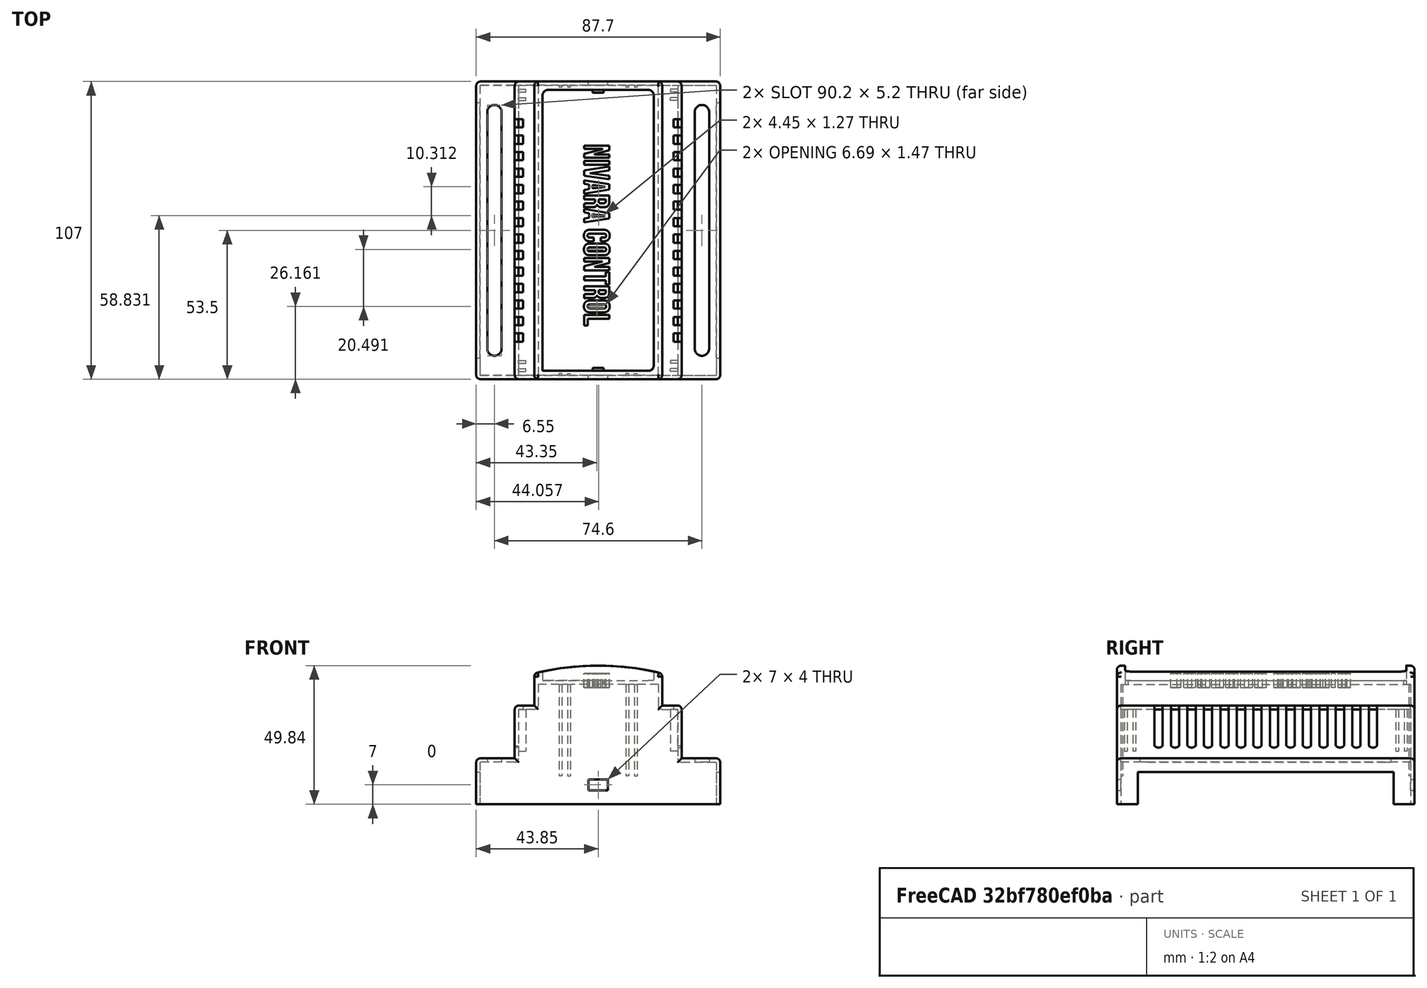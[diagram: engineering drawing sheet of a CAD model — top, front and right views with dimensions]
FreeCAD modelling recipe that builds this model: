
FCSTD DOCUMENT  (FreeCAD 1.0R39285 (Git))
Label: Diseño de la Pieza con su Etiqueta (2023-1283)
License: All rights reserved
LicenseURL: https://en.wikipedia.org/wiki/All_rights_reserved
objects: Sketcher::SketchObject×15, PartDesign::Pad×9, PartDesign::Mirrored×7, PartDesign::Pocket×6, PartDesign::Fillet×4, PartDesign::Thickness×2, PartDesign::Plane×1, PartDesign::Body×1, Part::Box×1, Part::Part2DObjectPython×1, Part::Extrusion×1, Part::Cut×1
note: 113 computed .brp shape members not serialized (recipe doc carries the construction recipe); baked Part::Feature solids carry a one-line shape summary decoded from their .brp

FEATURE [Sketcher::SketchObject] Sketch
  ArcFitTolerance = 1e-06
  AttachmentSupport = -> [XZ_Plane001]
  FullyConstrained = true
  MakeInternals = false
  MapMode = 5
  Placement = pos=(0,0,0) rot=(1,0,0;1.5708rad)
  sketch-geometry (12):
    g0: LineSegment StartX=-43.85 StartY=0 StartZ=0 EndX=43.85 EndY=0 EndZ=0
    g1: LineSegment StartX=-43.85 StartY=0 StartZ=0 EndX=-43.85 EndY=16.54 EndZ=0
    g2: LineSegment StartX=43.85 StartY=0 StartZ=0 EndX=43.85 EndY=16.54 EndZ=0
    g3: LineSegment StartX=-43.85 StartY=16.54 StartZ=0 EndX=-30 EndY=16.54 EndZ=0
    g4: LineSegment StartX=43.85 StartY=16.54 StartZ=0 EndX=30 EndY=16.54 EndZ=0
    g5: LineSegment StartX=-30 StartY=16.54 StartZ=0 EndX=-30 EndY=35.54 EndZ=0
    g6: LineSegment StartX=30 StartY=16.54 StartZ=0 EndX=30 EndY=35.54 EndZ=0
    g7: LineSegment StartX=-30 StartY=35.54 StartZ=0 EndX=-23 EndY=35.54 EndZ=0
    g8: LineSegment StartX=30 StartY=35.54 StartZ=0 EndX=23 EndY=35.54 EndZ=0
    g9: LineSegment StartX=23 StartY=35.54 StartZ=0 EndX=23 EndY=44.54 EndZ=0
    g10: LineSegment StartX=-23 StartY=35.54 StartZ=0 EndX=-23 EndY=44.54 EndZ=0
    g11: LineSegment StartX=-23 StartY=44.54 StartZ=0 EndX=23 EndY=44.54 EndZ=0
  constraints (36):
    c: Distance(g0) = 87.7
    c: PointOnObject(g0,g-1)
    c: PointOnObject(g0,g-1)
    c: Vertical(g1)
    c: Coincident(g1,g0)
    c: Vertical(g2)
    c: Coincident(g2,g0)
    c: Distance(g3) = 13.85
    c: Horizontal(g3)
    c: Coincident(g3,g1)
    c: Distance(g4) = 13.85
    c: Horizontal(g4)
    c: Coincident(g4,g2)
    c: Vertical(g5)
    c: Coincident(g5,g3)
    c: Vertical(g6)
    c: Coincident(g6,g4)
    c: Distance(g7) = 7
    c: Horizontal(g7)
    c: Coincident(g7,g5)
    c: Distance(g8) = 7
    c: Horizontal(g8)
    c: Coincident(g8,g6)
    c: Vertical(g9)
    c: Coincident(g9,g8)
    c: Vertical(g10)
    c: Coincident(g10,g7)
    c: Coincident(g11,g10)
    c: Coincident(g11,g9)
    c: Equal(g1,g2)
    c: Equal(g5,g6)
    c: Equal(g10,g9)
    c: Distance(g0,g11) = 44.54
    c: DistanceY(g1,g1) = 16.54
    c: Distance(g5,g0) = 35.54
    c: Distance(g10,g-2) = 23
FEATURE [PartDesign::Pad] Pad
  Direction = (0,-1,2e-16)
  Length = 107
  Length2 = 10
  Placement = pos=(0,0,0) rot=(1,0,0;1.5708rad)
  Profile = -> Sketch
  ReferenceAxis = -> Sketch [N_Axis]
  Refine = true
  Suppressed = false
  Type = 0
FEATURE [PartDesign::Thickness] Thickness
  Base = -> Pad
  BaseFeature = -> Pad
  Intersection = false
  Join = 0
  Mode = 0
  Placement = pos=(0,0,0) rot=(1,0,0;1.5708rad)
  Refine = true
  Reversed = true
  SupportTransform = false
  Suppressed = false
  Value = 1.4
FEATURE [PartDesign::Thickness] Thickness001
  Base = -> Thickness [Face1]
  BaseFeature = -> Thickness
  Intersection = false
  Join = 0
  Mode = 0
  Refine = true
  Reversed = true
  SupportTransform = false
  Suppressed = false
  Value = 1.4
FEATURE [Sketcher::SketchObject] Sketch001
  ArcFitTolerance = 1e-06
  AttachmentSupport = -> [Thickness001]
  FullyConstrained = true
  MakeInternals = false
  MapMode = 5
  Placement = pos=(-43.85,0,0) rot=(0.57735,-0.57735,-0.57735;2.0944rad)
  sketch-geometry (4):
    g0: LineSegment StartX=7.575 StartY=0 StartZ=0 EndX=99.425 EndY=0 EndZ=0
    g1: LineSegment StartX=99.425 StartY=0 StartZ=0 EndX=99.425 EndY=11.6 EndZ=0
    g2: LineSegment StartX=99.425 StartY=11.6 StartZ=0 EndX=7.575 EndY=11.6 EndZ=0
    g3: LineSegment StartX=7.575 StartY=11.6 StartZ=0 EndX=7.575 EndY=0 EndZ=0
  constraints (12):
    c: Coincident(g0,g1)
    c: Coincident(g1,g2)
    c: Coincident(g2,g3)
    c: Coincident(g3,g0)
    c: Horizontal(g0)
    c: Horizontal(g2)
    c: Vertical(g1)
    c: Vertical(g3)
    c: PointOnObject(g0,g-1)
    c: DistanceX(g2,g2) = 91.85
    c: DistanceY(g1,g1) = 11.6
    c: DistanceX(g-1,g0) = 7.575
FEATURE [PartDesign::Pocket] Pocket
  BaseFeature = -> Thickness001
  Direction = (1,0,0)
  Length = 5
  Length2 = 5
  Profile = -> Sketch001
  ReferenceAxis = -> Sketch001 [N_Axis]
  Refine = true
  Suppressed = false
  Type = 1
FEATURE [Sketcher::SketchObject] Sketch002
  ArcFitTolerance = 1e-06
  AttachmentSupport = -> [Pocket]
  FullyConstrained = true
  MakeInternals = false
  MapMode = 5
  Placement = pos=(0,4.2e-15,0) rot=(0,0.707107,0.707107;3.14159rad)
  sketch-geometry (4):
    g0: LineSegment StartX=-23 StartY=44.54 StartZ=0 EndX=23 EndY=44.54 EndZ=0
    g1: LineSegment StartX=-23 StartY=44.54 StartZ=0 EndX=-23 EndY=47.04 EndZ=0
    g2: LineSegment StartX=23 StartY=44.54 StartZ=0 EndX=23 EndY=47.04 EndZ=0
    g3: ArcOfCircle CenterX=1.7e-15 CenterY=-46.0243 CenterZ=0 NormalX=0 NormalY=0 NormalZ=1 AngleXU=0 Radius=95.8643 StartAngle=1.32851 EndAngle=1.81308
  constraints (13):
    c: Distance(g0) = 46
    c: Horizontal(g0)
    c: Distance(g-1,g0) = 44.54
    c: Distance(g0,g-2) = 23
    c: Distance(g1) = 2.5
    c: Coincident(g1,g0)
    c: Vertical(g1)
    c: Distance(g2) = 2.5
    c: Coincident(g2,g0)
    c: Vertical(g2)
    c: Coincident(g3,g1)
    c: Coincident(g3,g2)
    c: Distance(g3,g0) = -5.3
FEATURE [PartDesign::Pad] Pad001
  BaseFeature = -> Pocket
  Direction = (0,1,-2e-16)
  Length = 107
  Length2 = 10
  Profile = -> Sketch002
  ReferenceAxis = -> Sketch002 [N_Axis]
  Refine = true
  Suppressed = false
  Type = 0
FEATURE [Sketcher::SketchObject] Sketch003
  ArcFitTolerance = 1e-06
  AttachmentSupport = -> [Pad001]
  ExternalGeometry = -> [Pad001]
  FullyConstrained = true
  MakeInternals = false
  MapMode = 5
  Placement = pos=(0,4.2e-15,0) rot=(0,0.707107,0.707107;3.14159rad)
  sketch-geometry (4):
    g0: LineSegment StartX=-23 StartY=44.54 StartZ=0 EndX=-23 EndY=47.04 EndZ=0
    g1: LineSegment StartX=23 StartY=44.54 StartZ=0 EndX=23 EndY=47.04 EndZ=0
    g2: ArcOfCircle CenterX=4.82e-14 CenterY=-46.0243 CenterZ=0 NormalX=0 NormalY=0 NormalZ=1 AngleXU=0 Radius=95.8643 StartAngle=1.32851 EndAngle=1.81308
    g3: LineSegment StartX=-23 StartY=44.54 StartZ=0 EndX=23 EndY=44.54 EndZ=0
  constraints (9):
    c: Distance(g0) = 2.5
    c: Coincident(g2,g0)
    c: Coincident(g2,g1)
    c: Coincident(g3,g-3)
    c: Coincident(g3,g-3)
    c: Perpendicular(g0,g3) = 4.71239
    c: Distance(g2,g3) = -5.3
    c: Perpendicular(g1,g3) = 4.71239
    c: DistanceY(g1,g1) = 2.5
FEATURE [PartDesign::Pad] Pad002
  BaseFeature = -> Pad001
  Direction = (0,1,-2e-16)
  Length = 3
  Length2 = 10
  Profile = -> Sketch003
  ReferenceAxis = -> Sketch003 [N_Axis]
  Refine = true
  Reversed = true
  Suppressed = false
  Type = 0
FEATURE [Sketcher::SketchObject] Sketch004
  ArcFitTolerance = 1e-06
  AttachmentSupport = -> [Pad002]
  ExternalGeometry = -> [Pad002]
  FullyConstrained = true
  MakeInternals = false
  MapMode = 5
  Placement = pos=(0,-107,0) rot=(1,0,0;1.5708rad)
  sketch-geometry (4):
    g0: LineSegment StartX=-23 StartY=44.54 StartZ=0 EndX=23 EndY=44.54 EndZ=0
    g1: LineSegment StartX=23 StartY=44.54 StartZ=0 EndX=23 EndY=47.04 EndZ=0
    g2: LineSegment StartX=-23 StartY=44.54 StartZ=0 EndX=-23 EndY=47.04 EndZ=0
    g3: ArcOfCircle CenterX=3.7756e-12 CenterY=-46.0243 CenterZ=0 NormalX=0 NormalY=0 NormalZ=1 AngleXU=0 Radius=95.8643 StartAngle=1.32851 EndAngle=1.81308
  constraints (9):
    c: Coincident(g0,g-5)
    c: Coincident(g0,g-6)
    c: Coincident(g1,g0)
    c: Coincident(g1,g-6)
    c: Coincident(g2,g0)
    c: Coincident(g2,g-5)
    c: Coincident(g3,g2)
    c: Coincident(g3,g1)
    c: Tangent(g3,g-4)
FEATURE [PartDesign::Pad] Pad003
  BaseFeature = -> Pad002
  Direction = (0,-1,2e-16)
  Length = 3
  Length2 = 10
  Profile = -> Sketch004
  ReferenceAxis = -> Sketch004 [N_Axis]
  Refine = true
  Reversed = true
  Suppressed = false
  Type = 0
FEATURE [Sketcher::SketchObject] Sketch005
  ArcFitTolerance = 1e-06
  AttachmentSupport = -> [Pad003]
  ExternalGeometry = -> [Pad003]
  FullyConstrained = true
  MakeInternals = false
  MapMode = 5
  Placement = pos=(23,-8.5e-15,1.304e-13) rot=(0.57735,0.57735,0.57735;2.0944rad)
  sketch-geometry (4):
    g0: LineSegment StartX=-104 StartY=49.84 StartZ=0 EndX=-104 EndY=44.54 EndZ=0
    g1: LineSegment StartX=-104 StartY=44.54 StartZ=0 EndX=-3 EndY=44.54 EndZ=0
    g2: LineSegment StartX=-3 StartY=49.84 StartZ=0 EndX=-3 EndY=44.54 EndZ=0
    g3: LineSegment StartX=-104 StartY=49.84 StartZ=0 EndX=-3 EndY=49.84 EndZ=0
  constraints (8):
    c: Coincident(g0,g-5)
    c: Coincident(g0,g-3)
    c: Coincident(g1,g0)
    c: Coincident(g1,g-3)
    c: Coincident(g2,g-4)
    c: Coincident(g2,g1)
    c: Coincident(g3,g0)
    c: Coincident(g3,g2)
FEATURE [PartDesign::Pad] Pad004
  BaseFeature = -> Pad003
  Direction = (1,0,5.8e-15)
  Length = 3
  Length2 = 10
  Profile = -> Sketch005
  ReferenceAxis = -> Sketch005 [N_Axis]
  Refine = true
  Reversed = true
  Suppressed = false
  Type = 0
FEATURE [PartDesign::Mirrored] Mirrored
  BaseFeature = -> Pad004
  MirrorPlane = -> YZ_Plane001
  Originals = -> [Pad004]
  Refine = true
  Suppressed = false
  TransformMode = 0
FEATURE [Sketcher::SketchObject] Sketch006
  ArcFitTolerance = 1e-06
  AttachmentSupport = -> [Mirrored]
  FullyConstrained = true
  MakeInternals = false
  MapMode = 5
  Placement = pos=(0,7.3e-15,16.54) rot=(0,0,1;0rad)
  sketch-geometry (4):
    g0: ArcOfCircle CenterX=37.3 CenterY=-11 CenterZ=0 NormalX=0 NormalY=0 NormalZ=1 AngleXU=0 Radius=2.6 StartAngle=2.2037e-12 EndAngle=3.14159
    g1: ArcOfCircle CenterX=37.3 CenterY=-96 CenterZ=0 NormalX=0 NormalY=0 NormalZ=1 AngleXU=0 Radius=2.6 StartAngle=3.14159 EndAngle=6.28319
    g2: LineSegment StartX=39.9 StartY=-11 StartZ=0 EndX=39.9 EndY=-96 EndZ=0
    g3: LineSegment StartX=34.7 StartY=-11 StartZ=0 EndX=34.7 EndY=-96 EndZ=0
  constraints (10):
    c: Tangent(g0,g2) = 1.5708
    c: Tangent(g0,g3) = -1.5708
    c: Tangent(g1,g2) = 1.5708
    c: Tangent(g1,g3) = -1.5708
    c: Equal(g0,g1)
    c: Vertical(g2)
    c: Distance(g2,g3) = 5.2
    c: DistanceY(g2,g2) = 85
    c: Distance(g0,g-2) = 37.3
    c: Distance(g0,g-1) = 11
FEATURE [PartDesign::Pocket] Pocket001
  BaseFeature = -> Mirrored
  Direction = (0,0,-1)
  Length = 5
  Length2 = 5
  Profile = -> Sketch006
  ReferenceAxis = -> Sketch006 [N_Axis]
  Refine = true
  Suppressed = false
  Type = 0
FEATURE [PartDesign::Mirrored] Mirrored001
  BaseFeature = -> Pocket001
  MirrorPlane = -> YZ_Plane001
  Originals = -> [Pocket001]
  Refine = true
  Suppressed = false
  TransformMode = 0
FEATURE [Sketcher::SketchObject] Sketch007
  ArcFitTolerance = 1e-06
  AttachmentSupport = -> [Mirrored001]
  ExternalGeometry = -> [Mirrored001]
  FullyConstrained = true
  MakeInternals = false
  MapMode = 5
  Placement = pos=(30,0,0) rot=(0.57735,0.57735,0.57735;2.0944rad)
  sketch-geometry (57):
    g0: LineSegment [constr] StartX=-53.5 StartY=35.54 StartZ=0 EndX=-53.5 EndY=16.54 EndZ=0
    g1: LineSegment StartX=-16.4625 StartY=35.54 StartZ=0 EndX=-13.4995 EndY=35.54 EndZ=0
    g2: LineSegment StartX=-13.4995 StartY=35.54 StartZ=0 EndX=-13.4995 EndY=21.04 EndZ=0
    g3: LineSegment StartX=-16.4625 StartY=35.54 StartZ=0 EndX=-16.4625 EndY=21.04 EndZ=0
    g4: ArcOfCircle CenterX=-14.981 CenterY=22.3836 CenterZ=0 NormalX=0 NormalY=0 NormalZ=1 AngleXU=0 Radius=2 StartAngle=3.8782 EndAngle=5.54658
    g5: LineSegment StartX=-22.3885 StartY=35.54 StartZ=0 EndX=-19.4255 EndY=35.54 EndZ=0
    g6: LineSegment StartX=-19.4255 StartY=35.54 StartZ=0 EndX=-19.4255 EndY=21.04 EndZ=0
    g7: LineSegment StartX=-22.3885 StartY=35.54 StartZ=0 EndX=-22.3885 EndY=21.04 EndZ=0
    g8: ArcOfCircle CenterX=-20.907 CenterY=22.3836 CenterZ=0 NormalX=0 NormalY=0 NormalZ=1 AngleXU=0 Radius=2 StartAngle=3.8782 EndAngle=5.54658
    g9: LineSegment StartX=-28.3145 StartY=35.54 StartZ=0 EndX=-25.3515 EndY=35.54 EndZ=0
    g10: LineSegment StartX=-25.3515 StartY=35.54 StartZ=0 EndX=-25.3515 EndY=21.04 EndZ=0
    g11: LineSegment StartX=-28.3145 StartY=35.54 StartZ=0 EndX=-28.3145 EndY=21.04 EndZ=0
    g12: ArcOfCircle CenterX=-26.833 CenterY=22.3836 CenterZ=0 NormalX=0 NormalY=0 NormalZ=1 AngleXU=0 Radius=2 StartAngle=3.8782 EndAngle=5.54658
    g13: LineSegment StartX=-34.2405 StartY=35.54 StartZ=0 EndX=-31.2775 EndY=35.54 EndZ=0
    g14: LineSegment StartX=-34.2405 StartY=35.54 StartZ=0 EndX=-34.2405 EndY=21.04 EndZ=0
    g15: LineSegment StartX=-31.2775 StartY=35.54 StartZ=0 EndX=-31.2775 EndY=21.04 EndZ=0
    g16: ArcOfCircle CenterX=-32.759 CenterY=22.3836 CenterZ=0 NormalX=0 NormalY=0 NormalZ=1 AngleXU=0 Radius=2 StartAngle=3.8782 EndAngle=5.54658
    g17: LineSegment StartX=-40.1665 StartY=35.54 StartZ=0 EndX=-37.2035 EndY=35.54 EndZ=0
    g18: LineSegment StartX=-37.2035 StartY=35.54 StartZ=0 EndX=-37.2035 EndY=21.04 EndZ=0
    g19: LineSegment StartX=-40.1665 StartY=35.54 StartZ=0 EndX=-40.1665 EndY=21.04 EndZ=0
    g20: ArcOfCircle CenterX=-38.685 CenterY=22.3836 CenterZ=0 NormalX=0 NormalY=0 NormalZ=1 AngleXU=0 Radius=2 StartAngle=3.8782 EndAngle=5.54658
    g21: LineSegment StartX=-46.0925 StartY=35.54 StartZ=0 EndX=-43.1295 EndY=35.54 EndZ=0
    g22: LineSegment StartX=-43.1295 StartY=35.54 StartZ=0 EndX=-43.1295 EndY=21.04 EndZ=0
    g23: LineSegment StartX=-46.0925 StartY=35.54 StartZ=0 EndX=-46.0925 EndY=21.04 EndZ=0
    g24: ArcOfCircle CenterX=-44.611 CenterY=22.3836 CenterZ=0 NormalX=0 NormalY=0 NormalZ=1 AngleXU=0 Radius=2 StartAngle=3.8782 EndAngle=5.54658
    g25: LineSegment StartX=-52.0185 StartY=35.54 StartZ=0 EndX=-49.0555 EndY=35.54 EndZ=0
    g26: LineSegment StartX=-49.0555 StartY=35.54 StartZ=0 EndX=-49.0555 EndY=21.04 EndZ=0
    g27: LineSegment StartX=-52.0185 StartY=35.54 StartZ=0 EndX=-52.0185 EndY=21.04 EndZ=0
    g28: ArcOfCircle CenterX=-50.537 CenterY=22.3836 CenterZ=0 NormalX=0 NormalY=0 NormalZ=1 AngleXU=0 Radius=2 StartAngle=3.8782 EndAngle=5.54658
    g29: LineSegment StartX=-57.9445 StartY=35.54 StartZ=0 EndX=-54.9815 EndY=35.54 EndZ=0
    g30: LineSegment StartX=-54.9815 StartY=35.54 StartZ=0 EndX=-54.9815 EndY=21.04 EndZ=0
    g31: LineSegment StartX=-57.9445 StartY=35.54 StartZ=0 EndX=-57.9445 EndY=21.04 EndZ=0
    g32: ArcOfCircle CenterX=-56.463 CenterY=22.3836 CenterZ=0 NormalX=0 NormalY=0 NormalZ=1 AngleXU=0 Radius=2 StartAngle=3.8782 EndAngle=5.54658
    g33: LineSegment StartX=-63.8705 StartY=35.54 StartZ=0 EndX=-60.9075 EndY=35.54 EndZ=0
    g34: LineSegment StartX=-60.9075 StartY=35.54 StartZ=0 EndX=-60.9075 EndY=21.04 EndZ=0
    g35: LineSegment StartX=-63.8705 StartY=35.54 StartZ=0 EndX=-63.8705 EndY=21.04 EndZ=0
    g36: ArcOfCircle CenterX=-62.389 CenterY=22.3836 CenterZ=0 NormalX=0 NormalY=0 NormalZ=1 AngleXU=0 Radius=2 StartAngle=3.8782 EndAngle=5.54658
    g37: LineSegment StartX=-69.7965 StartY=35.54 StartZ=0 EndX=-66.8335 EndY=35.54 EndZ=0
    g38: LineSegment StartX=-66.8335 StartY=35.54 StartZ=0 EndX=-66.8335 EndY=21.04 EndZ=0
    g39: LineSegment StartX=-69.7965 StartY=35.54 StartZ=0 EndX=-69.7965 EndY=21.04 EndZ=0
    g40: ArcOfCircle CenterX=-68.315 CenterY=22.3836 CenterZ=0 NormalX=0 NormalY=0 NormalZ=1 AngleXU=0 Radius=2 StartAngle=3.8782 EndAngle=5.54658
    g41: LineSegment StartX=-75.7225 StartY=35.54 StartZ=0 EndX=-72.7595 EndY=35.54 EndZ=0
    g42: LineSegment StartX=-72.7595 StartY=35.54 StartZ=0 EndX=-72.7595 EndY=21.04 EndZ=0
    g43: LineSegment StartX=-75.7225 StartY=35.54 StartZ=0 EndX=-75.7225 EndY=21.04 EndZ=0
    g44: ArcOfCircle CenterX=-74.241 CenterY=22.3836 CenterZ=0 NormalX=0 NormalY=0 NormalZ=1 AngleXU=0 Radius=2 StartAngle=3.8782 EndAngle=5.54658
    g45: LineSegment StartX=-81.6485 StartY=35.54 StartZ=0 EndX=-78.6855 EndY=35.54 EndZ=0
    g46: LineSegment StartX=-78.6855 StartY=35.54 StartZ=0 EndX=-78.6855 EndY=21.04 EndZ=0
    g47: LineSegment StartX=-81.6485 StartY=35.54 StartZ=0 EndX=-81.6485 EndY=21.04 EndZ=0
    g48: ArcOfCircle CenterX=-80.167 CenterY=22.3836 CenterZ=0 NormalX=0 NormalY=0 NormalZ=1 AngleXU=0 Radius=2 StartAngle=3.8782 EndAngle=5.54658
    g49: LineSegment StartX=-87.5745 StartY=35.54 StartZ=0 EndX=-84.6115 EndY=35.54 EndZ=0
    g50: LineSegment StartX=-84.6115 StartY=35.54 StartZ=0 EndX=-84.6115 EndY=21.04 EndZ=0
    g51: LineSegment StartX=-87.5745 StartY=35.54 StartZ=0 EndX=-87.5745 EndY=21.04 EndZ=0
    g52: ArcOfCircle CenterX=-86.093 CenterY=22.3836 CenterZ=0 NormalX=0 NormalY=0 NormalZ=1 AngleXU=0 Radius=2 StartAngle=3.8782 EndAngle=5.54658
    g53: LineSegment StartX=-93.5005 StartY=35.54 StartZ=0 EndX=-90.5375 EndY=35.54 EndZ=0
    g54: LineSegment StartX=-90.5375 StartY=35.54 StartZ=0 EndX=-90.5375 EndY=21.04 EndZ=0
    g55: LineSegment StartX=-93.5005 StartY=35.54 StartZ=0 EndX=-93.5005 EndY=21.04 EndZ=0
    g56: ArcOfCircle CenterX=-92.019 CenterY=22.3836 CenterZ=0 NormalX=0 NormalY=0 NormalZ=1 AngleXU=0 Radius=2 StartAngle=3.8782 EndAngle=5.54658
  constraints (184):
    c: Symmetric(g-4,g-4,g0)
    c: Symmetric(g-3,g-3,g0)
    c: PointOnObject(g1,g-4)
    c: PointOnObject(g1,g-4)
    c: Distance(g2) = 14.5
    c: Vertical(g2)
    c: Coincident(g2,g1)
    c: Vertical(g3)
    c: Coincident(g3,g1)
    c: Coincident(g4,g3)
    c: Coincident(g4,g2)
    c: DistanceX(g1,g1) = 2.963
    c: Radius(g4) = 2
    c: Distance(g5) = 2.963
    c: Horizontal(g5)
    c: PointOnObject(g5,g-4)
    c: Vertical(g6)
    c: Coincident(g6,g5)
    c: Vertical(g7)
    c: Coincident(g7,g5)
    c: Equal(g2,g3)
    c: Equal(g3,g6)
    c: Equal(g6,g7)
    c: Distance(g3,g6) = 2.963
    c: Coincident(g8,g7)
    c: Coincident(g8,g6)
    c: Equal(g4,g8)
    c: Horizontal(g9)
    c: PointOnObject(g9,g-4)
    c: Vertical(g10)
    c: Coincident(g10,g9)
    c: Vertical(g11)
    c: Coincident(g11,g9)
    c: Coincident(g12,g11)
    c: Coincident(g12,g10)
    c: Equal(g5,g9)
    c: Equal(g6,g10)
    c: Equal(g10,g11)
    c: Equal(g4,g12)
    c: Distance(g7,g10) = 2.963
    c: PointOnObject(g13,g-4)
    c: PointOnObject(g13,g-4)
    c: Vertical(g14)
    c: Coincident(g14,g13)
    c: Vertical(g15)
    c: Coincident(g15,g13)
    c: Coincident(g16,g14)
    c: Coincident(g16,g15)
    c: Equal(g15,g14)
    c: Equal(g14,g2)
    c: Equal(g1,g13)
    c: Distance(g11,g15) = 2.963
    c: Equal(g4,g16)
    c: PointOnObject(g17,g-4)
    c: PointOnObject(g17,g-4)
    c: Vertical(g18)
    c: Coincident(g18,g17)
    c: Vertical(g19)
    c: Coincident(g19,g17)
    c: Coincident(g20,g19)
    c: Coincident(g20,g18)
    c: Distance(g14,g18) = 2.963
    c: Equal(g2,g18)
    c: Equal(g18,g19)
    c: Equal(g1,g17)
    c: Equal(g4,g20)
    c: PointOnObject(g21,g-4)
    c: PointOnObject(g21,g-4)
    c: Vertical(g22)
    c: Coincident(g22,g21)
    c: Vertical(g23)
    c: Coincident(g23,g21)
    c: Coincident(g24,g23)
    c: Coincident(g24,g22)
    c: Equal(g1,g21)
    c: Equal(g22,g23)
    c: Equal(g23,g2)
    c: Distance(g19,g22) = 2.963
    c: Equal(g4,g24)
    c: PointOnObject(g25,g-4)
    c: PointOnObject(g25,g-4)
    c: Vertical(g26)
    c: Coincident(g26,g25)
    c: Vertical(g27)
    c: Coincident(g27,g25)
    c: Coincident(g28,g27)
    c: Coincident(g28,g26)
    c: Equal(g2,g26)
    c: Equal(g26,g27)
    c: Equal(g1,g25)
    c: Equal(g4,g28)
    c: Distance(g23,g26) = 2.963
    c: PointOnObject(g29,g-4)
    c: PointOnObject(g29,g-4)
    c: Coincident(g30,g29)
    c: Vertical(g30)
    c: Coincident(g31,g29)
    c: Vertical(g31)
    c: Equal(g30,g31)
    c: Equal(g31,g3)
    c: Coincident(g32,g31)
    c: Coincident(g32,g30)
    c: Equal(g4,g32)
    c: Equal(g29,g1)
    c: Distance(g27,g30) = 2.963
    c: PointOnObject(g33,g-4)
    c: PointOnObject(g33,g-4)
    c: Coincident(g34,g33)
    c: Vertical(g34)
    c: Coincident(g35,g33)
    c: Vertical(g35)
    c: Equal(g35,g34)
    c: Equal(g34,g31)
    c: Equal(g33,g29)
    c: Coincident(g36,g35)
    c: Coincident(g36,g34)
    c: Equal(g32,g36)
    c: Distance(g31,g34) = 2.963
    c: PointOnObject(g37,g-4)
    c: PointOnObject(g37,g-4)
    c: Coincident(g38,g37)
    c: Vertical(g38)
    c: Coincident(g39,g37)
    c: Vertical(g39)
    c: Coincident(g40,g39)
    c: Coincident(g40,g38)
    c: Equal(g38,g39)
    c: Equal(g39,g35)
    c: Equal(g40,g36)
    c: Equal(g33,g37)
    c: Distance(g35,g38) = 2.963
    c: PointOnObject(g41,g-4)
    c: PointOnObject(g41,g-4)
    c: Coincident(g42,g41)
    c: Vertical(g42)
    c: Coincident(g43,g41)
    c: Vertical(g43)
    c: Coincident(g44,g43)
    c: Coincident(g44,g42)
    c: Equal(g43,g42)
    c: Equal(g42,g39)
    c: Equal(g41,g37)
    c: Equal(g44,g40)
    c: Distance(g39,g42) = 2.963
    c: PointOnObject(g45,g-4)
    c: PointOnObject(g45,g-4)
    c: Coincident(g46,g45)
    c: Vertical(g46)
    c: Coincident(g47,g45)
    c: Vertical(g47)
    c: Coincident(g48,g47)
    c: Coincident(g48,g46)
    c: Equal(g47,g46)
    c: Equal(g46,g43)
    c: Equal(g45,g41)
    c: Equal(g44,g48)
    c: Distance(g43,g46) = 2.963
    c: PointOnObject(g49,g-4)
    c: PointOnObject(g49,g-4)
    c: Coincident(g50,g49)
    c: Vertical(g50)
    c: Coincident(g51,g49)
    c: Vertical(g51)
    c: Coincident(g52,g51)
    c: Coincident(g52,g50)
    c: Equal(g51,g50)
    c: Equal(g50,g47)
    c: Equal(g49,g45)
    c: Equal(g48,g52)
    c: Distance(g47,g50) = 2.963
    c: PointOnObject(g53,g-4)
    c: PointOnObject(g53,g-4)
    c: Coincident(g54,g53)
    c: Vertical(g54)
    c: Coincident(g55,g53)
    c: Vertical(g55)
    c: Coincident(g56,g55)
    c: Coincident(g56,g54)
    c: Equal(g55,g54)
    c: Equal(g54,g51)
    c: Equal(g56,g52)
    c: Equal(g53,g49)
    c: Distance(g51,g54) = 2.963
    c: Distance(g0,g27) = 1.4815
FEATURE [PartDesign::Pocket] Pocket002
  BaseFeature = -> Mirrored001
  Direction = (-1,0,0)
  Length = 2.963
  Length2 = 5
  Profile = -> Sketch007
  ReferenceAxis = -> Sketch007 [N_Axis]
  Refine = true
  Suppressed = false
  Type = 0
FEATURE [PartDesign::Mirrored] Mirrored002
  BaseFeature = -> Pocket002
  MirrorPlane = -> YZ_Plane001
  Originals = -> [Pocket002]
  Refine = true
  Suppressed = false
  TransformMode = 0
FEATURE [PartDesign::Fillet] Fillet
  Base = -> Mirrored002 [Edge272,Edge110,Edge99,Edge166,Edge114,Edge118,Edge122,Edge126,Edge130,Edge134,Edge138,Edge142,Edge146,Edge150,Edge154,Edge158,Edge162,Edge20,Edge98,Edge97,Edge96]
  BaseFeature = -> Mirrored002
  Radius = 1.5
  Refine = true
  SupportTransform = false
  Suppressed = false
  UseAllEdges = false
FEATURE [PartDesign::Mirrored] Mirrored003
  BaseFeature = -> Fillet
  MirrorPlane = -> YZ_Plane001
  Originals = -> [Fillet]
  Refine = true
  Suppressed = false
  TransformMode = 0
FEATURE [Sketcher::SketchObject] Sketch008
  ArcFitTolerance = 1e-06
  AttachmentSupport = -> [Mirrored003]
  FullyConstrained = true
  MakeInternals = false
  MapMode = 5
  Placement = pos=(0,-107,3.53e-14) rot=(1,0,0;1.5708rad)
  sketch-geometry (4):
    g0: LineSegment StartX=-3.5 StartY=9 StartZ=0 EndX=3.5 EndY=9 EndZ=0
    g1: LineSegment StartX=-3.5 StartY=9 StartZ=0 EndX=-3.5 EndY=5 EndZ=0
    g2: LineSegment StartX=3.5 StartY=9 StartZ=0 EndX=3.5 EndY=5 EndZ=0
    g3: LineSegment StartX=-3.5 StartY=5 StartZ=0 EndX=3.5 EndY=5 EndZ=0
  constraints (12):
    c: Distance(g0) = 7
    c: Horizontal(g0)
    c: Vertical(g1)
    c: Coincident(g1,g0)
    c: Distance(g2) = 4
    c: Vertical(g2)
    c: Coincident(g2,g0)
    c: Coincident(g3,g1)
    c: Coincident(g3,g2)
    c: Distance(g-2,g1) = 3.5
    c: Equal(g2,g1)
    c: Distance(g-1,g3) = 5
FEATURE [PartDesign::Pocket] Pocket003
  BaseFeature = -> Mirrored003
  Direction = (0,1,-2e-16)
  Length = 5
  Length2 = 5
  Profile = -> Sketch008
  ReferenceAxis = -> Sketch008 [N_Axis]
  Refine = true
  Suppressed = false
  Type = 1
FEATURE [Sketcher::SketchObject] Sketch009
  ArcFitTolerance = 1e-06
  AttachmentSupport = -> [Pocket003]
  ExternalGeometry = -> [Pocket003]
  FullyConstrained = true
  MakeInternals = false
  MapMode = 5
  Placement = pos=(0,-104,0) rot=(1,0,0;1.5708rad)
  sketch-geometry (8):
    g0: LineSegment StartX=-23 StartY=47.04 StartZ=0 EndX=-23 EndY=49.84 EndZ=0
    g1: LineSegment StartX=-23 StartY=49.84 StartZ=0 EndX=-20 EndY=49.84 EndZ=0
    g2: LineSegment StartX=-20 StartY=49.84 StartZ=0 EndX=-20 EndY=47.7305 EndZ=0
    g3: ArcOfCircle CenterX=9.71783e-05 CenterY=-46.0247 CenterZ=0 NormalX=0 NormalY=0 NormalZ=1 AngleXU=0 Radius=95.8647 StartAngle=1.78097 EndAngle=1.81308
    g4: LineSegment StartX=20 StartY=49.84 StartZ=0 EndX=23 EndY=49.84 EndZ=0
    g5: LineSegment StartX=23 StartY=49.84 StartZ=0 EndX=23 EndY=47.04 EndZ=0
    g6: LineSegment StartX=20 StartY=49.84 StartZ=0 EndX=20 EndY=47.7305 EndZ=0
    g7: ArcOfCircle CenterX=-7.58465e-05 CenterY=-46.0246 CenterZ=0 NormalX=0 NormalY=0 NormalZ=1 AngleXU=0 Radius=95.8646 StartAngle=1.32851 EndAngle=1.36062
  constraints (19):
    c: Coincident(g0,g-6)
    c: Coincident(g0,g-6)
    c: Coincident(g1,g0)
    c: Coincident(g1,g-5)
    c: Coincident(g2,g1)
    c: Coincident(g2,g-4)
    c: Coincident(g3,g0)
    c: Coincident(g3,g2)
    c: Tangent(g3,g-3)
    c: Coincident(g4,g-8)
    c: Coincident(g4,g-9)
    c: Coincident(g5,g4)
    c: PointOnObject(g5,g-10)
    c: Vertical(g5)
    c: Coincident(g6,g4)
    c: Coincident(g6,g-10)
    c: Coincident(g7,g6)
    c: Coincident(g7,g5)
    c: Tangent(g7,g-10)
FEATURE [PartDesign::Pocket] Pocket004
  BaseFeature = -> Pocket003
  Direction = (0,1,-2e-16)
  Length = 0
  Length2 = 5
  Profile = -> Sketch009
  ReferenceAxis = -> Sketch009 [N_Axis]
  Refine = true
  Suppressed = false
  Type = 3
  UpToFace = -> Pocket003 [Face89]
FEATURE [PartDesign::Mirrored] Mirrored004
  BaseFeature = -> Pocket004
  MirrorPlane = -> YZ_Plane001
  Originals = -> [Fillet]
  Refine = true
  Suppressed = false
  TransformMode = 0
FEATURE [PartDesign::Fillet] Fillet001
  Base = -> Mirrored004 [Edge26,Edge28,Edge32,Edge34,Edge33,Edge5,Edge22,Edge24,Edge25,Edge29]
  BaseFeature = -> Mirrored004
  Radius = 1.5
  Refine = true
  SupportTransform = false
  Suppressed = false
  UseAllEdges = false
FEATURE [Sketcher::SketchObject] Sketch010
  ArcFitTolerance = 1e-06
  FullyConstrained = true
  MakeInternals = false
  MapMode = 5
  Placement = pos=(0,1.96e-14,44.54) rot=(0,0,1;0rad)
  sketch-geometry (8):
    g0: LineSegment StartX=-2 StartY=-3 StartZ=0 EndX=2 EndY=-3 EndZ=0
    g1: LineSegment StartX=-2 StartY=-3 StartZ=0 EndX=-2 EndY=-4 EndZ=0
    g2: LineSegment StartX=2 StartY=-3 StartZ=0 EndX=2 EndY=-4 EndZ=0
    g3: LineSegment StartX=-2 StartY=-4 StartZ=0 EndX=2 EndY=-4 EndZ=0
    g4: LineSegment StartX=2 StartY=-104 StartZ=0 EndX=-2 EndY=-104 EndZ=0
    g5: LineSegment StartX=2 StartY=-104 StartZ=0 EndX=2 EndY=-103 EndZ=0
    g6: LineSegment StartX=-2 StartY=-104 StartZ=0 EndX=-2 EndY=-103 EndZ=0
    g7: LineSegment StartX=2 StartY=-103 StartZ=0 EndX=-2 EndY=-103 EndZ=0
  constraints (24):
    c: PointOnObject(g0,g-3)
    c: PointOnObject(g0,g-3)
    c: Distance(g1) = 1
    c: Vertical(g1)
    c: Coincident(g1,g0)
    c: Distance(g2) = 1
    c: Vertical(g2)
    c: Coincident(g2,g0)
    c: Coincident(g3,g1)
    c: Coincident(g3,g2)
    c: Distance(g-2,g1) = 2
    c: Distance(g0,g0) = 4
    c: PointOnObject(g4,g-4)
    c: PointOnObject(g4,g-4)
    c: Distance(g5) = 1
    c: Vertical(g5)
    c: Coincident(g5,g4)
    c: Distance(g6) = 1
    c: Vertical(g6)
    c: Coincident(g6,g4)
    c: Coincident(g7,g5)
    c: Coincident(g7,g6)
    c: Distance(g-2,g5) = 2
    c: DistanceX(g4,g4) = 4
FEATURE [PartDesign::Pocket] Pocket005
  BaseFeature = -> Fillet001
  Direction = (0,0,-1)
  Length = 5
  Length2 = 5
  Profile = -> Sketch010
  ReferenceAxis = -> Sketch010 [N_Axis]
  Refine = true
  Suppressed = false
  Type = 0
FEATURE [PartDesign::Fillet] Fillet002
  Base = -> Pocket005 [Edge3,Edge78,Edge86,Edge10]
  BaseFeature = -> Pocket005
  Radius = 1.5
  Refine = true
  SupportTransform = false
  Suppressed = false
  UseAllEdges = false
FEATURE [Sketcher::SketchObject] Sketch011
  ArcFitTolerance = 1e-06
  FullyConstrained = true
  MakeInternals = false
  MapMode = 5
  Placement = pos=(0,-105.6,0) rot=(0,0.707107,0.707107;3.14159rad)
  sketch-geometry (9):
    g0: LineSegment [constr] StartX=-12 StartY=43.14 StartZ=0 EndX=-12 EndY=10.2 EndZ=0
    g1: LineSegment StartX=-11 StartY=43.14 StartZ=0 EndX=-11 EndY=10.2 EndZ=0
    g2: LineSegment StartX=-10 StartY=43.14 StartZ=0 EndX=-10 EndY=10.2 EndZ=0
    g3: LineSegment StartX=-11 StartY=10.2 StartZ=0 EndX=-10 EndY=10.2 EndZ=0
    g4: LineSegment StartX=-11 StartY=43.14 StartZ=0 EndX=-10 EndY=43.14 EndZ=0
    g5: LineSegment StartX=-13 StartY=43.14 StartZ=0 EndX=-13 EndY=10.2 EndZ=0
    g6: LineSegment StartX=-14 StartY=43.14 StartZ=0 EndX=-14 EndY=10.2 EndZ=0
    g7: LineSegment StartX=-13 StartY=10.2 StartZ=0 EndX=-14 EndY=10.2 EndZ=0
    g8: LineSegment StartX=-13 StartY=43.14 StartZ=0 EndX=-14 EndY=43.14 EndZ=0
  constraints (25):
    c: Distance(g0) = 32.94
    c: Vertical(g0)
    c: PointOnObject(g0,g-3)
    c: Distance(g-2,g0) = 12
    c: PointOnObject(g1,g-3)
    c: Vertical(g1)
    c: PointOnObject(g2,g-3)
    c: Vertical(g2)
    c: Equal(g2,g0)
    c: Distance(g3) = 1
    c: Coincident(g3,g1)
    c: Perpendicular(g2,g3) = 1.5708
    c: Coincident(g4,g1)
    c: Coincident(g4,g2)
    c: Distance(g1,g0) = 1
    c: Vertical(g5)
    c: Vertical(g6)
    c: Distance(g7) = 1
    c: Coincident(g7,g5)
    c: Perpendicular(g6,g7) = 4.71239
    c: Coincident(g8,g5)
    c: Coincident(g8,g6)
    c: Symmetric(g1,g5,g0)
    c: Equal(g0,g1)
    c: Equal(g6,g0)
FEATURE [PartDesign::Pad] Pad005
  BaseFeature = -> Fillet002
  Direction = (0,1,-2e-16)
  Length = 0.63
  Length2 = 10
  Profile = -> Sketch011
  ReferenceAxis = -> Sketch011 [N_Axis]
  Refine = true
  Suppressed = false
  Type = 0
FEATURE [PartDesign::Mirrored] Mirrored005
  BaseFeature = -> Pad005
  MirrorPlane = -> YZ_Plane001
  Originals = -> [Pad005]
  Refine = true
  Suppressed = false
  TransformMode = 0
FEATURE [Sketcher::SketchObject] Sketch012
  ArcFitTolerance = 1e-06
  AttachmentSupport = -> [Mirrored005]
  ExternalGeometry = -> [Mirrored005]
  FullyConstrained = true
  MakeInternals = false
  MapMode = 5
  Placement = pos=(0,-1.4,0) rot=(1,0,0;1.5708rad)
  sketch-geometry (16):
    g0: LineSegment StartX=-14 StartY=43.14 StartZ=0 EndX=-13 EndY=43.14 EndZ=0
    g1: LineSegment StartX=-11 StartY=43.14 StartZ=0 EndX=-10 EndY=43.14 EndZ=0
    g2: LineSegment StartX=-14 StartY=43.14 StartZ=0 EndX=-14 EndY=10.2 EndZ=0
    g3: LineSegment StartX=-14 StartY=10.2 StartZ=0 EndX=-13 EndY=10.2 EndZ=0
    g4: LineSegment StartX=-13 StartY=10.2 StartZ=0 EndX=-13 EndY=43.14 EndZ=0
    g5: LineSegment StartX=-11 StartY=43.14 StartZ=0 EndX=-11 EndY=10.2 EndZ=0
    g6: LineSegment StartX=-11 StartY=10.2 StartZ=0 EndX=-10 EndY=10.2 EndZ=0
    g7: LineSegment StartX=-10 StartY=10.2 StartZ=0 EndX=-10 EndY=43.14 EndZ=0
    g8: LineSegment StartX=10 StartY=43.14 StartZ=0 EndX=11 EndY=43.14 EndZ=0
    g9: LineSegment StartX=10 StartY=43.14 StartZ=0 EndX=10 EndY=10.2 EndZ=0
    g10: LineSegment StartX=10 StartY=10.2 StartZ=0 EndX=11 EndY=10.2 EndZ=0
    g11: LineSegment StartX=11 StartY=10.2 StartZ=0 EndX=11 EndY=43.14 EndZ=0
    g12: LineSegment StartX=13 StartY=43.14 StartZ=0 EndX=14 EndY=43.14 EndZ=0
    g13: LineSegment StartX=13 StartY=43.14 StartZ=0 EndX=13 EndY=10.2 EndZ=0
    g14: LineSegment StartX=13 StartY=10.2 StartZ=0 EndX=14 EndY=10.2 EndZ=0
    g15: LineSegment StartX=14 StartY=10.2 StartZ=0 EndX=14 EndY=43.14 EndZ=0
  constraints (32):
    c: Coincident(g0,g-16)
    c: Coincident(g0,g-15)
    c: Coincident(g1,g-13)
    c: Coincident(g1,g-14)
    c: Coincident(g2,g0)
    c: Coincident(g2,g-18)
    c: Coincident(g3,g2)
    c: Coincident(g3,g-18)
    c: Coincident(g4,g3)
    c: Coincident(g4,g0)
    c: Coincident(g5,g1)
    c: Coincident(g5,g-17)
    c: Coincident(g6,g5)
    c: Coincident(g6,g-17)
    c: Coincident(g7,g6)
    c: Coincident(g7,g1)
    c: Coincident(g8,g-7)
    c: Coincident(g8,g-8)
    c: Coincident(g9,g8)
    c: Coincident(g9,g-10)
    c: Coincident(g10,g9)
    c: Coincident(g10,g-10)
    c: Coincident(g11,g10)
    c: Coincident(g11,g8)
    c: Coincident(g12,g-5)
    c: Coincident(g12,g-5)
    c: Coincident(g13,g12)
    c: Coincident(g13,g-9)
    c: Coincident(g14,g13)
    c: Coincident(g14,g-9)
    c: Coincident(g15,g14)
    c: Coincident(g15,g12)
FEATURE [PartDesign::Pad] Pad006
  BaseFeature = -> Mirrored005
  Direction = (0,-1,2e-16)
  Length = 0.63
  Length2 = 10
  Profile = -> Sketch012
  ReferenceAxis = -> Sketch012 [N_Axis]
  Refine = true
  Suppressed = false
  Type = 0
FEATURE [Sketcher::SketchObject] Sketch013
  ArcFitTolerance = 1e-06
  AttachmentSupport = -> [Pad006]
  ExternalGeometry = -> [Pad006]
  FullyConstrained = true
  MakeInternals = false
  MapMode = 5
  Placement = pos=(28.6,0,0) rot=(0.57735,-0.57735,-0.57735;2.0944rad)
  sketch-geometry (9):
    g0: LineSegment [constr] StartX=4.76 StartY=34.14 StartZ=0 EndX=4.76 EndY=19.14 EndZ=0
    g1: LineSegment StartX=2.76 StartY=34.14 StartZ=0 EndX=3.76 EndY=34.14 EndZ=0
    g2: LineSegment StartX=2.76 StartY=34.14 StartZ=0 EndX=2.76 EndY=19.14 EndZ=0
    g3: LineSegment StartX=3.76 StartY=34.14 StartZ=0 EndX=3.76 EndY=19.14 EndZ=0
    g4: LineSegment StartX=2.76 StartY=19.14 StartZ=0 EndX=3.76 EndY=19.14 EndZ=0
    g5: LineSegment StartX=6.76 StartY=34.14 StartZ=0 EndX=6.76 EndY=19.14 EndZ=0
    g6: LineSegment StartX=6.76 StartY=19.14 StartZ=0 EndX=5.76 EndY=19.14 EndZ=0
    g7: LineSegment StartX=5.76 StartY=34.14 StartZ=0 EndX=5.76 EndY=19.14 EndZ=0
    g8: LineSegment StartX=6.76 StartY=34.14 StartZ=0 EndX=5.76 EndY=34.14 EndZ=0
  constraints (27):
    c: Vertical(g0)
    c: PointOnObject(g0,g-3)
    c: Distance(g0,g-4) = 3.36
    c: Distance(g1) = 1
    c: Horizontal(g1)
    c: PointOnObject(g1,g-3)
    c: Vertical(g2)
    c: Coincident(g2,g1)
    c: Distance(g3) = 15
    c: Vertical(g3)
    c: Coincident(g3,g1)
    c: Coincident(g4,g2)
    c: Coincident(g4,g3)
    c: Equal(g0,g3)
    c: Equal(g3,g2)
    c: Distance(g0,g3) = 1
    c: Distance(g8) = 1
    c: Horizontal(g8)
    c: Vertical(g5)
    c: Coincident(g5,g8)
    c: Distance(g7) = 15
    c: Vertical(g7)
    c: Coincident(g7,g8)
    c: Coincident(g6,g5)
    c: Coincident(g6,g7)
    c: Equal(g7,g5)
    c: Symmetric(g6,g3,g0)
FEATURE [PartDesign::Pad] Pad007
  BaseFeature = -> Pad006
  Direction = (-1,0,0)
  Length = 2.66
  Length2 = 10
  Profile = -> Sketch013
  ReferenceAxis = -> Sketch013 [N_Axis]
  Refine = true
  Suppressed = false
  Type = 0
FEATURE [PartDesign::Plane] DatumPlane
  AttachmentOffset = pos=(0,0,53.5) rot=(0,0,1;0rad)
  AttachmentSupport = -> [Sketch013]
  Length = 91.037
  MapMode = 4
  Placement = pos=(28.6,-53.5,0) rot=(0.57735,-0.57735,0.57735;2.0944rad)
  ResizeMode = 0
  Width = 103.902
FEATURE [PartDesign::Mirrored] Mirrored006
  BaseFeature = -> Pad007
  MirrorPlane = -> DatumPlane
  Originals = -> [Pad007]
  Refine = true
  Suppressed = false
  TransformMode = 0
FEATURE [Sketcher::SketchObject] Sketch014
  ArcFitTolerance = 1e-06
  AttachmentSupport = -> [Mirrored006]
  ExternalGeometry = -> [Mirrored006]
  FullyConstrained = true
  MakeInternals = false
  MapMode = 5
  Placement = pos=(-28.6,0,0) rot=(0.57735,0.57735,0.57735;2.0944rad)
  sketch-geometry (16):
    g0: LineSegment StartX=-104.24 StartY=34.14 StartZ=0 EndX=-103.24 EndY=34.14 EndZ=0
    g1: LineSegment StartX=-104.24 StartY=34.14 StartZ=0 EndX=-104.24 EndY=19.14 EndZ=0
    g2: LineSegment StartX=-104.24 StartY=19.14 StartZ=0 EndX=-103.24 EndY=19.14 EndZ=0
    g3: LineSegment StartX=-103.24 StartY=19.14 StartZ=0 EndX=-103.24 EndY=34.14 EndZ=0
    g4: LineSegment StartX=-101.24 StartY=34.14 StartZ=0 EndX=-100.24 EndY=34.14 EndZ=0
    g5: LineSegment StartX=-101.24 StartY=34.14 StartZ=0 EndX=-101.24 EndY=19.14 EndZ=0
    g6: LineSegment StartX=-101.24 StartY=19.14 StartZ=0 EndX=-100.24 EndY=19.14 EndZ=0
    g7: LineSegment StartX=-100.24 StartY=19.14 StartZ=0 EndX=-100.24 EndY=34.14 EndZ=0
    g8: LineSegment StartX=-6.76 StartY=34.14 StartZ=0 EndX=-5.76 EndY=34.14 EndZ=0
    g9: LineSegment StartX=-6.76 StartY=34.14 StartZ=0 EndX=-6.76 EndY=19.14 EndZ=0
    g10: LineSegment StartX=-6.76 StartY=19.14 StartZ=0 EndX=-5.76 EndY=19.14 EndZ=0
    g11: LineSegment StartX=-5.76 StartY=19.14 StartZ=0 EndX=-5.76 EndY=34.14 EndZ=0
    g12: LineSegment StartX=-3.76 StartY=34.14 StartZ=0 EndX=-2.76 EndY=34.14 EndZ=0
    g13: LineSegment StartX=-3.76 StartY=34.14 StartZ=0 EndX=-3.76 EndY=19.14 EndZ=0
    g14: LineSegment StartX=-3.76 StartY=19.14 StartZ=0 EndX=-2.76 EndY=19.14 EndZ=0
    g15: LineSegment StartX=-2.76 StartY=19.14 StartZ=0 EndX=-2.76 EndY=34.14 EndZ=0
  constraints (32):
    c: Coincident(g0,g-6)
    c: Coincident(g0,g-6)
    c: Coincident(g1,g0)
    c: Coincident(g1,g-5)
    c: Coincident(g2,g1)
    c: Coincident(g2,g-4)
    c: Coincident(g3,g2)
    c: Coincident(g3,g0)
    c: Coincident(g4,g-9)
    c: Coincident(g4,g-8)
    c: Coincident(g5,g4)
    c: Coincident(g5,g-10)
    c: Coincident(g6,g5)
    c: Coincident(g6,g-10)
    c: Coincident(g7,g6)
    c: Coincident(g7,g4)
    c: Coincident(g8,g-14)
    c: Coincident(g8,g-14)
    c: Coincident(g9,g8)
    c: Coincident(g9,g-13)
    c: Coincident(g10,g9)
    c: Coincident(g10,g-12)
    c: Coincident(g11,g10)
    c: Coincident(g11,g8)
    c: Coincident(g12,g-17)
    c: Coincident(g12,g-16)
    c: Coincident(g13,g12)
    c: Coincident(g13,g-18)
    c: Coincident(g14,g13)
    c: Coincident(g14,g-18)
    c: Coincident(g15,g14)
    c: Coincident(g15,g12)
FEATURE [PartDesign::Pad] Pad008
  BaseFeature = -> Mirrored006
  Direction = (1,0,0)
  Length = 2.66
  Length2 = 10
  Profile = -> Sketch014
  ReferenceAxis = -> Sketch014 [N_Axis]
  Refine = true
  Suppressed = false
  Type = 0
FEATURE [PartDesign::Fillet] Fillet003
  Base = -> Pad008 [Edge379,Edge371,Edge373]
  BaseFeature = -> Pad008
  Radius = 2
  Refine = true
  SupportTransform = false
  Suppressed = false
  UseAllEdges = false
FEATURE [PartDesign::Body] Body001
  AllowCompound = false
  Group = -> [Sketch,Pad,Thickness,Thickness001,Sketch001,Pocket,Sketch002,Pad001,Sketch003,Pad002,Sketch004,Pad003,Sketch005,Pad004,Mirrored,Sketch006,Pocket001,Mirrored001,Sketch007,Pocket002,Mirrored002,Fillet,Mirrored003,Sketch008,Pocket003,Sketch009,Pocket004,Mirrored004,Fillet001,Sketch010,Pocket005,Fillet002,Sketch011,Pad005,Mirrored005,Sketch012,Pad006,Sketch013,Pad007,DatumPlane,Mirrored006,Sketch014,+2 more]
  Origin = -> Origin001
  Tip = -> Fillet003
FEATURE [Part::Box] Box  label="Cubo"
  AttacherType = Attacher::AttachEngine3D
  Height = 15
  Length = 75
  Placement = pos=(-30,-12,-17) rot=(0,0,1;0rad)
  Width = 40
FEATURE [Part::Part2DObjectPython] ShapeString  # Draft 2D object (typed FeaturePython)
  FontFile = <userpath>/Downloads/Bebas_Neue/BebasNeue-Regular.ttf
  Fuse = false
  Justification = 6
  JustificationReference = 0
  KeepLeftMargin = false
  MakeFace = true
  ObliqueAngle = 0
  Placement = pos=(-25,5,1) rot=(0,0,1;0rad)
  ScaleToSize = true
  Size = 9
  String = NIVARA CONTROL
  Tracking = 0
FEATURE [Part::Extrusion] Extrude
  Base = -> ShapeString
  Dir = (0,0,1)
  DirMode = 2
  FaceMakerClass = Part::FaceMakerBullseye
  FaceMakerMode = 3
  LengthFwd = 5
  LengthRev = 0
  Solid = false
  Symmetric = false
FEATURE [Part::Cut] Cut
  Base = -> Extrude
  Placement = pos=(-10,-48,41) rot=(0,0,1;4.71239rad)
  Tool = -> Box
